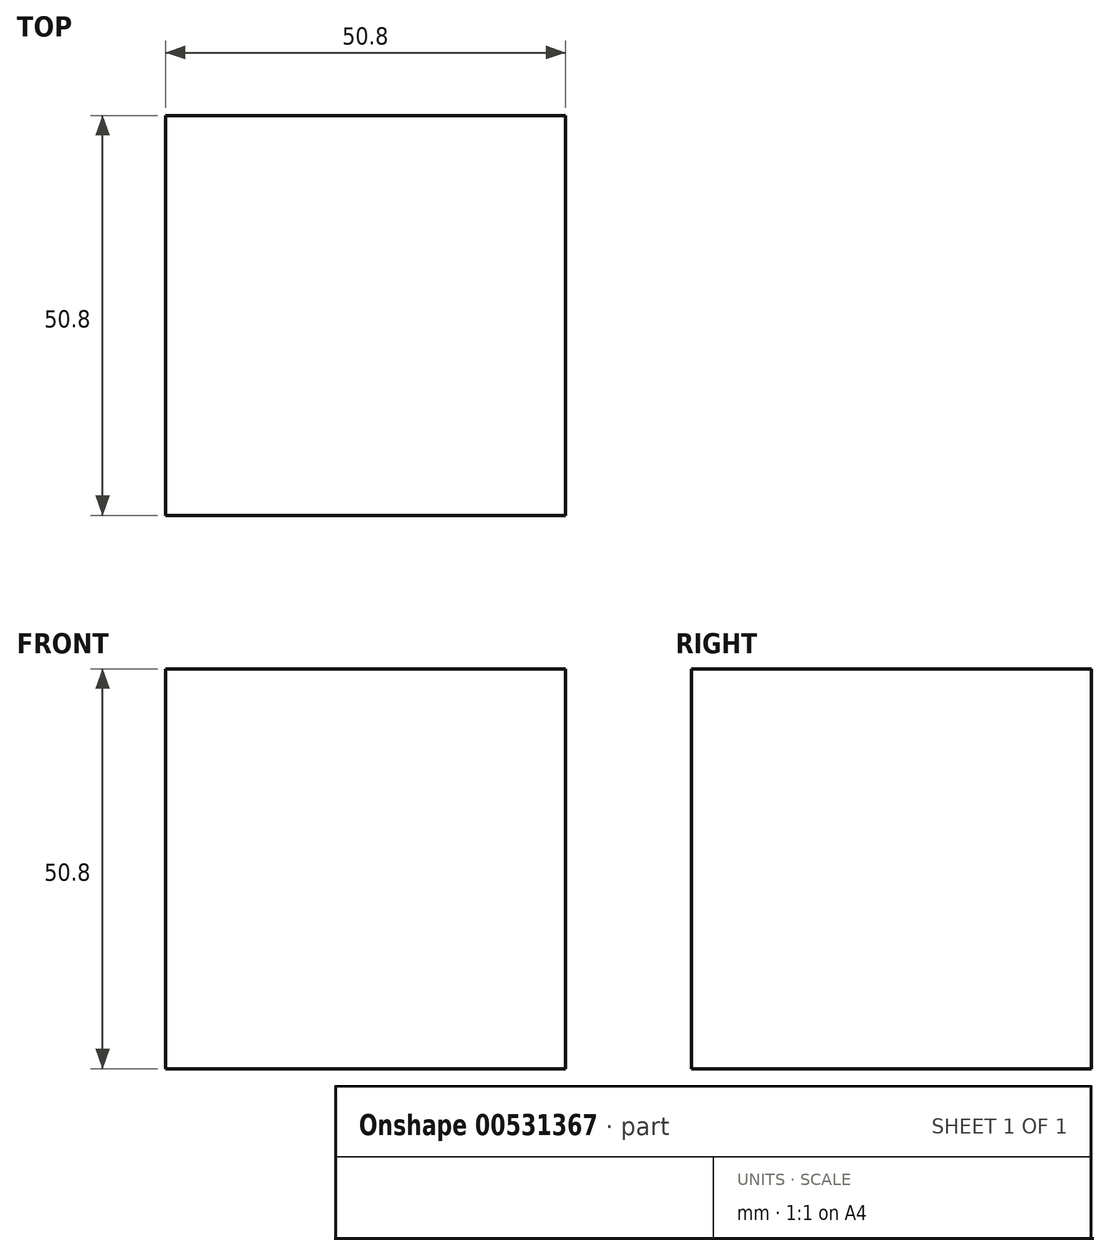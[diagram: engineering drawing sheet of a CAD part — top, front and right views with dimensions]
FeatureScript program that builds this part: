
annotation { "Feature Type Name" : "Feature", "Feature Type Description" : "" }
export const myFeature = defineFeature(function(context is Context, id is Id, definition is map)
    precondition{}
    {
        {
            var Q0;
            Q0=qCreatedBy(makeId("Front.planeOp"),FACE);
            var sketch = newSketch(context, id + "F0", { "sketchPlane" : qUnion([Q0])});
            skLineSegment(sketch, "E0", {"start": v(0, 0) * mm, "end": v(50.8, 0) * mm});
            skLineSegment(sketch, "E1", {"start": v(50.8, 0) * mm, "end": v(50.8, 50.8) * mm});
            skLineSegment(sketch, "E2", {"start": v(50.8, 50.8) * mm, "end": v(0, 50.8) * mm});
            skLineSegment(sketch, "E3", {"start": v(0, 50.8) * mm, "end": v(0, 0) * mm});
            skSolve(sketch);
        }
        {
            var Q0;
            Q0 = qSketchRegion(id + "F0", true);
            extrude(context, id + "F1", {"entities" : qUnion([Q0]), "depth" : 50.8 * mm, "offsetDistance" : 25.4 * mm});
        }
    });
